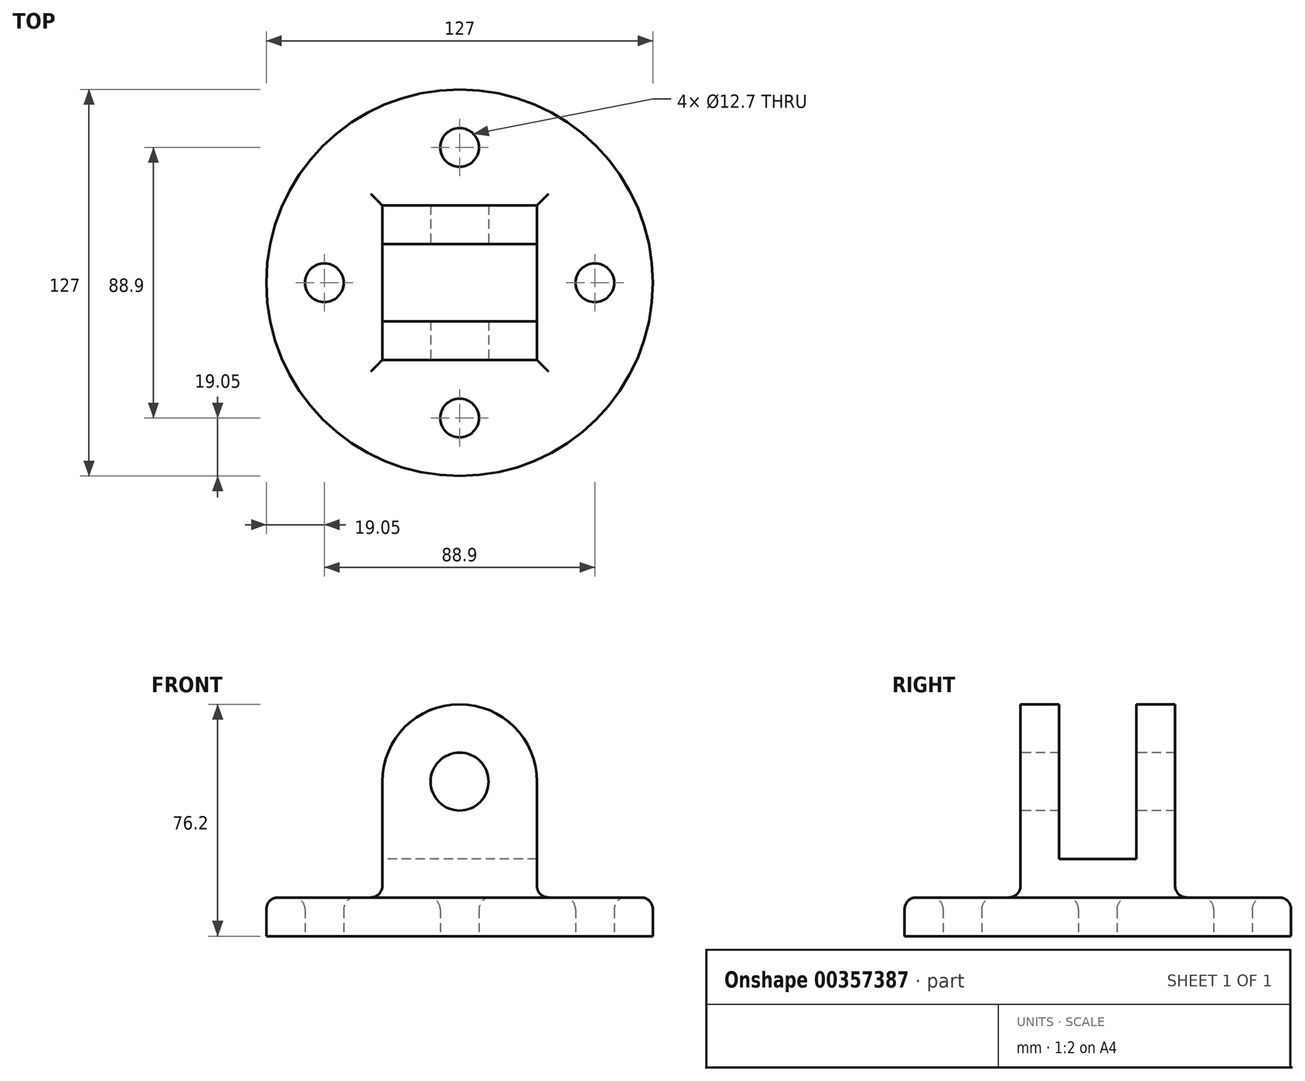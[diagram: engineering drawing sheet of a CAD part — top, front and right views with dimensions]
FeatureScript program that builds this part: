
annotation { "Feature Type Name" : "Feature", "Feature Type Description" : "" }
export const myFeature = defineFeature(function(context is Context, id is Id, definition is map)
    precondition{}
    {
        {
            var Q0;
            Q0=qCreatedBy(makeId("Top.planeOp"),FACE);
            var sketch = newSketch(context, id + "F0", { "sketchPlane" : qUnion([Q0])});
            skCircle(sketch, "E0", {"center": v(0, 0) * mm, "radius": 63.5 * mm});
            skCircle(sketch, "E1", {"center": v(0, 44.45) * mm, "radius": 6.35 * mm});
            skCircle(sketch, "E2", {"center": v(44.45, 0) * mm, "radius": 6.35 * mm});
            skCircle(sketch, "E3", {"center": v(0, -44.45) * mm, "radius": 6.35 * mm});
            skCircle(sketch, "E4", {"center": v(-44.45, 0) * mm, "radius": 6.35 * mm});
            skSolve(sketch);
        }
        {
            var Q0;
            Q0=makeQuery(id+"F0.imprint","IMPRINT",FACE,{"disambiguationData":[TD([[makeQuery(id+"F0.imprint","IMPRINT",EDGE,{"derivedFrom":sQuery(id+"F0.wireOp",EDGE,"E0")}),1.0]])]});
            extrude(context, id + "F1", {"entities" : qUnion([Q0]), "depth" : 12.7 * mm});
        }
        {
            var Q0;
            Q0=makeQuery(id+"F1.opExtrude","CAP_FACE",FACE,{"disambiguationData":[OSD([sQuery(id+"F0.wireOp",EDGE,"E0"),sQuery(id+"F0.wireOp",EDGE,"E1"),sQuery(id+"F0.wireOp",EDGE,"E2"),sQuery(id+"F0.wireOp",EDGE,"E3"),sQuery(id+"F0.wireOp",EDGE,"E4")])],"isStart":false});
            var sketch = newSketch(context, id + "F2", { "sketchPlane" : qUnion([Q0])});
            skLineSegment(sketch, "E5.bottom", {"start": v(25.4, 25.4) * mm, "end": v(-25.4, 25.4) * mm});
            skLineSegment(sketch, "E5.top", {"start": v(25.4, -25.4) * mm, "end": v(-25.4, -25.4) * mm});
            skLineSegment(sketch, "E5.left", {"start": v(25.4, 25.4) * mm, "end": v(25.4, -25.4) * mm});
            skLineSegment(sketch, "E5.right", {"start": v(-25.4, 25.4) * mm, "end": v(-25.4, -25.4) * mm});
            skPoint(sketch, "E5.middle", {"position": v(0, 0) * mm});
            skSolve(sketch);
        }
        {
            var Q0;
            Q0 = qSketchRegion(id + "F2", true);
            extrude(context, id + "F3", {"entities" : qUnion([Q0]), "operationType" : NewBodyOperationType.ADD, "depth" : 63.5 * mm});
        }
        {
            var Q0;
            Q0=makeQuery(id+"F3.opExtrude","SWEPT_FACE",FACE,{"disambiguationData":[OSD([sQuery(id+"F2.wireOp",EDGE,"E5.top")])]});
            var sketch = newSketch(context, id + "F4", { "sketchPlane" : qUnion([Q0])});
            skPoint(sketch, "E6", {"position": v(0, 50.8) * mm});
            skPoint(sketch, "E6.positionSnap0", {"position": v(0, 12.7) * mm});
            skArc(sketch, "E7", {"start": v(25.4, 50.8) * mm, "mid": v(0, 76.2) * mm, "end": v(-25.4, 50.8) * mm});
            skCircle(sketch, "E8", {"center": v(0, 50.8) * mm, "radius": 9.53 * mm});
            skSolve(sketch);
        }
        {
            var Q0;
            {var subQ0=sQuery(id+"F4.wireOp",EDGE,"E7");var subQ1=sQuery(id+"F2.wireOp",EDGE,"E5.top");var subQ4=makeQuery(id+"F3.opExtrude","CAP_EDGE",EDGE,{"disambiguationData":[OSD([subQ1])],"isStart":false});var subQ5=makeQuery(id+"F4.imprint","INTERSECT",VERTEX,{"derivedFrom":[subQ4,subQ0]});Q0=makeQuery(id+"F4.imprint","IMPRINT",FACE,{"disambiguationData":[TD([[makeQuery(id+"F4.imprint","IMPRINT",EDGE,{"disambiguationData":[TD([[subQ5,-1.0]])],"derivedFrom":subQ0}),-1.0]])]});}
            var Q1;
            {var subQ0=sQuery(id+"F4.wireOp",EDGE,"E7");var subQ1=sQuery(id+"F2.wireOp",EDGE,"E5.top");var subQ4=makeQuery(id+"F3.opExtrude","CAP_EDGE",EDGE,{"disambiguationData":[OSD([subQ1])],"isStart":false});var subQ5=makeQuery(id+"F4.imprint","INTERSECT",VERTEX,{"derivedFrom":[subQ4,subQ0]});Q1=makeQuery(id+"F4.imprint","IMPRINT",FACE,{"disambiguationData":[TD([[makeQuery(id+"F4.imprint","IMPRINT",EDGE,{"disambiguationData":[TD([[subQ5,1.0]])],"derivedFrom":subQ0}),-1.0]])]});}
            var Q2;
            Q2=makeQuery(id+"F4.imprint","IMPRINT",FACE,{"disambiguationData":[TD([[makeQuery(id+"F4.imprint","IMPRINT",EDGE,{"derivedFrom":sQuery(id+"F4.wireOp",EDGE,"E8")}),1.0]])]});
            var Q3;
            Q3=makeQuery(id+"F3.opExtrude","SWEPT_FACE",FACE,{"disambiguationData":[OSD([sQuery(id+"F2.wireOp",EDGE,"E5.bottom")])]});
            extrude(context, id + "F5", {"entities" : qUnion([Q0, Q1, Q2]), "operationType" : NewBodyOperationType.REMOVE, "endBound" : BoundingType.UP_TO_SURFACE, "oppositeDirection" : true, "endBoundEntityFace" : qUnion([Q3]), "depth" : 25.4 * mm});
        }
        {
            var Q0;
            Q0=makeQuery(id+"F3.opExtrude","SWEPT_FACE",FACE,{"disambiguationData":[OSD([sQuery(id+"F2.wireOp",EDGE,"E5.right")])]});
            var sketch = newSketch(context, id + "F6", { "sketchPlane" : qUnion([Q0])});
            skPoint(sketch, "E9", {"position": v(0, 25.4) * mm});
            skPoint(sketch, "E9.positionSnap0", {"position": v(0, 12.7) * mm});
            skLineSegment(sketch, "E10.bottom", {"start": v(12.7, 76.2) * mm, "end": v(-12.7, 76.2) * mm});
            skLineSegment(sketch, "E10.left", {"start": v(12.7, 76.2) * mm, "end": v(12.7, 25.4) * mm});
            skLineSegment(sketch, "E10.right", {"start": v(-12.7, 76.2) * mm, "end": v(-12.7, 25.4) * mm});
            skLineSegment(sketch, "E11", {"start": v(-12.7, 25.4) * mm, "end": v(12.7, 25.4) * mm});
            skPoint(sketch, "E10.top.end.orphan", {"position": v(-12.7, -25.4) * mm});
            skPoint(sketch, "E10.top.start.orphan", {"position": v(12.7, -25.4) * mm});
            skSolve(sketch);
        }
        {
            var Q0;
            Q0 = qSketchRegion(id + "F6", true);
            var Q1;
            Q1=makeQuery(id+"F3.opExtrude","SWEPT_FACE",FACE,{"disambiguationData":[OSD([sQuery(id+"F2.wireOp",EDGE,"E5.left")])]});
            extrude(context, id + "F7", {"entities" : qUnion([Q0]), "operationType" : NewBodyOperationType.REMOVE, "endBound" : BoundingType.UP_TO_SURFACE, "oppositeDirection" : true, "endBoundEntityFace" : qUnion([Q1]), "depth" : 25.4 * mm});
        }
        {
            var Q0;
            Q0=makeQuery(id+"F1.opExtrude","CAP_FACE",FACE,{"disambiguationData":[OSD([sQuery(id+"F0.wireOp",EDGE,"E0"),sQuery(id+"F0.wireOp",EDGE,"E1"),sQuery(id+"F0.wireOp",EDGE,"E2"),sQuery(id+"F0.wireOp",EDGE,"E3"),sQuery(id+"F0.wireOp",EDGE,"E4")])],"isStart":false});
            fillet(context, id + "F8", {"entities" : qUnion([Q0]), "radius" : 3.8 * mm, "tangentPropagation" : true, "allowEdgeOverflow" : false});
        }
    });
